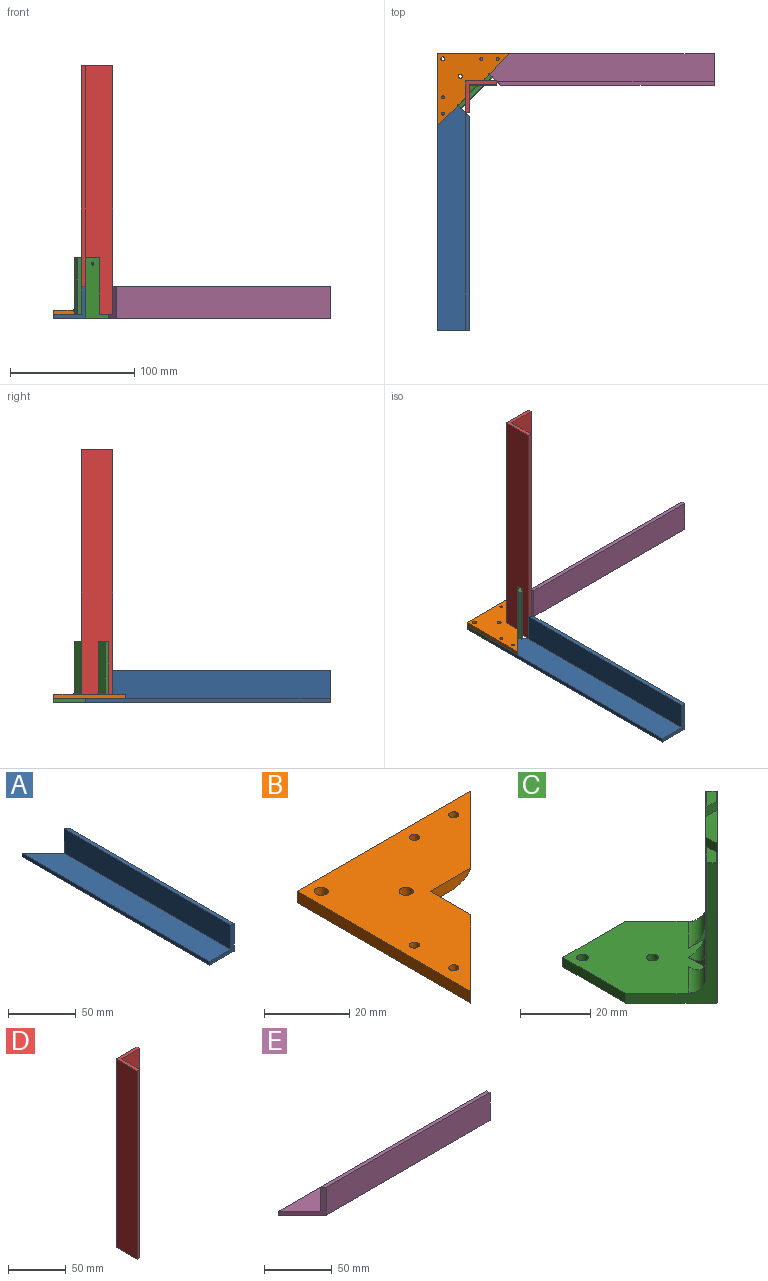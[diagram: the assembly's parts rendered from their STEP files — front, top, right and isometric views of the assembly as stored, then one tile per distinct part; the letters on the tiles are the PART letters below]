
ASSEMBLY  parts=5 mates=4
PART A: 8 faces, bbox 25.3x196.8x25.3 mm
  f0: plane 25.3x25.3mm, normal (0.71,0.71,0), area 214.5mm2, adj f2,f3,f4,f5,f6,f7
  f1: plane 25.3x25.3mm, normal (0,-1,0), area 151.7mm2, adj f2,f3,f4,f5,f6,f7
  f2: plane 174.7x3.2mm, normal (0,0,1), area 553.9mm2, adj f0,f1,f3,f7
  f3: plane 174.7x22.1mm, normal (-1,0,0), area 3860.9mm2, adj f0,f1,f2,f4
  f4: plane 196.8x22.1mm, normal (0,0,1), area 4105.1mm2, adj f0,f1,f3,f5
  f5: plane 196.8x3.2mm, normal (-1,0,0), area 629.8mm2, adj f0,f1,f4,f6
  f6: plane 196.8x25.3mm, normal (0,0,-1), area 4659mm2, adj f0,f1,f5,f7
  f7: plane 171.5x25.3mm, normal (1,0,0), area 4339mm2, adj f0,f1,f2,f6
PART B: 18 faces, bbox 57.7x57.7x3.3 mm
  f0: cylinder r=5mm len=12.56mm, axis (-0.71,-0.71,0), area 63.5mm2, adj f1,f5,f6,f9
  f1: plane 13.47x3.3mm, normal (1,0,0), area 38.5mm2, adj f0,f2,f5,f6
  f2: plane 13.47x3.3mm, normal (0,-1,0), area 38.5mm2, adj f1,f5,f6,f7
  f3: plane 57.67x3.3mm, normal (0,1,0), area 190.3mm2, adj f4,f5,f6,f11
  f4: plane 57.67x3.3mm, normal (-1,0,0), area 190.3mm2, adj f3,f5,f6,f8
  f5: plane 57.67x57.67mm, normal (0,0,1), area 1537mm2, adj f0,f1,f2,f3,f4,f7,f8,f11
  f6: plane 57.67x57.67mm, normal (0,0,-1), area 1436.3mm2, adj f0,f1,f2,f3,f4,f7,f8,f9
  f7: cylinder r=5mm len=12.56mm, axis (0.71,0.71,0), area 63.5mm2, adj f2,f5,f6,f10
  f8: plane 16.19x16.19mm, normal (0.71,-0.71,0), area 75.5mm2, adj f4,f5,f6,f9
  f9: plane 3.33x3.33mm, normal (0.71,0.71,0), area 4.2mm2, adj f0,f6,f8
  f10: plane 3.33x3.33mm, normal (-0.71,-0.71,0), area 4.2mm2, adj f6,f7,f11
  f11: plane 16.19x16.19mm, normal (0.71,-0.71,0), area 75.5mm2, adj f3,f5,f6,f10
  f12: cylinder r=1.65mm len=3.3mm, axis (0,0,1), area 34.2mm2, adj f5,f6
  f13: cylinder r=1.65mm len=3.3mm, axis (0,0,1), area 34.2mm2, adj f5,f6
  f14: cylinder r=1.2mm len=3.3mm, axis (0,0,1), area 24.9mm2, adj f5,f6
  f15: cylinder r=1.2mm len=3.3mm, axis (0,0,1), area 24.9mm2, adj f5,f6
  f16: cylinder r=1.2mm len=3.3mm, axis (0,0,1), area 24.9mm2, adj f5,f6
  f17: cylinder r=1.2mm len=3.3mm, axis (0,0,1), area 24.9mm2, adj f5,f6
PART C: 39 faces, bbox 48.3x48.3x49.1 mm
  f0: plane 40.24x40.24mm, normal (0,0,1), area 1018.2mm2, adj f1,f2,f3,f4,f5,f7,f8,f11
  f1: plane 48.75x18.34mm, normal (-0.71,-0.71,0), area 219.2mm2, adj f0,f5,f6,f21,f24,f26,f37
  f2: plane 49x24.95mm, normal (0.71,-0.71,0), area 1308.1mm2, adj f0,f6,f7,f8,f10,f11,f14,f19
  f3: plane 48.75x18.34mm, normal (0.71,0.71,0), area 219.2mm2, adj f0,f4,f6,f27,f30,f33,f35
  f4: plane 25.3x3.3mm, normal (0,1,0), area 83.5mm2, adj f0,f3,f5,f6
  f5: plane 25.3x3.3mm, normal (-1,0,0), area 83.5mm2, adj f0,f1,f4,f6
  f6: plane 43.72x43.72mm, normal (0,0,-1), area 1240mm2, adj f1,f2,f3,f4,f5,f17,f18,f21
  f7: plane 45.7x11.74mm, normal (-1,0,0), area 220.9mm2, adj f0,f2,f9,f10,f38
  f8: plane 45.7x11.74mm, normal (0,1,0), area 220.9mm2, adj f0,f2,f9,f10,f38
  f9: plane 40.7x7.07mm, normal (-0.71,0.71,0), area 402.5mm2, adj f7,f8,f10,f19,f38
  f10: plane 11.74x11.74mm, normal (0,0,1), area 43.9mm2, adj f2,f7,f8,f9
  f11: plane 45.81x11.84mm, normal (0,-1,0), area 220.8mm2, adj f0,f2,f12,f13,f28,f31,f34
  f12: plane 40.45x5.74mm, normal (-0.71,0.71,0), area 328.2mm2, adj f11,f31,f33,f34
  f13: plane 7.54x5.56mm, normal (0,0,1), area 18.1mm2, adj f11,f28,f30,f31
  f14: plane 45.81x11.84mm, normal (1,0,0), area 220.8mm2, adj f0,f2,f15,f16,f20,f23,f36
  f15: plane 40.45x5.74mm, normal (-0.71,0.71,0), area 328.2mm2, adj f14,f23,f26,f36
  f16: plane 7.54x5.56mm, normal (0,0,1), area 18.1mm2, adj f14,f20,f23,f24
  f17: cylinder r=1.65mm len=3.3mm, axis (0,0,-1), area 34.2mm2, adj f0,f6
  f18: cylinder r=1.65mm len=3.3mm, axis (0,0,-1), area 34.2mm2, adj f0,f6
  f19: cylinder r=1.2mm len=4.03mm, axis (0.71,-0.71,0), area 24.9mm2, adj f2,f9
  f20: cylinder r=0.25mm len=3.76mm, axis (-0.71,-0.71,0), area 1.9mm2, adj f2,f14,f16,f22
  f21: cylinder r=0.25mm len=48.75mm, axis (0,0,1), area 19.1mm2, adj f1,f2,f6,f22
  f22: sphere r=0.25mm, area 0.1mm2, adj f20,f21,f24
  f23: cylinder r=0.25mm len=5.91mm, axis (0.71,0.71,0), area 3.1mm2, adj f14,f15,f16,f25
  f24: cylinder r=0.25mm len=2.16mm, axis (-0.71,0.71,0), area 1.1mm2, adj f1,f16,f22,f25
  f25: sphere r=0.25mm, area 0.1mm2, adj f23,f24,f26
  f26: cylinder r=0.25mm len=40.45mm, axis (0,0,1), area 15.9mm2, adj f1,f15,f25,f37
  f27: cylinder r=0.25mm len=48.75mm, axis (0,0,-1), area 19.1mm2, adj f2,f3,f6,f29
  f28: cylinder r=0.25mm len=3.76mm, axis (-0.71,-0.71,0), area 1.9mm2, adj f2,f11,f13,f29
  f29: sphere r=0.25mm, area 0.1mm2, adj f27,f28,f30
  f30: cylinder r=0.25mm len=2.16mm, axis (0.71,-0.71,0), area 1.1mm2, adj f3,f13,f29,f32
  f31: cylinder r=0.25mm len=5.91mm, axis (0.71,0.71,0), area 3.1mm2, adj f11,f12,f13,f32
  f32: sphere r=0.25mm, area 0.1mm2, adj f30,f31,f33
  f33: cylinder r=0.25mm len=40.45mm, axis (0,0,1), area 15.9mm2, adj f3,f12,f32,f35
  f34: cylinder r=5mm len=12.81mm, axis (0.71,0.71,0), area 78mm2, adj f0,f11,f12,f35
  f35: torus R=5.25mm, axis (0,0,1), area 2.1mm2, adj f0,f3,f33,f34
  f36: cylinder r=5mm len=12.81mm, axis (0.71,0.71,0), area 78mm2, adj f0,f14,f15,f37
  f37: torus R=5.25mm, axis (0,0,1), area 2.1mm2, adj f0,f1,f26,f36
  f38: cylinder r=5mm len=10.61mm, axis (0.71,0.71,0), area 50mm2, adj f7,f8,f9
PART D: 8 faces, bbox 25.3x25.3x200 mm
  f0: plane 200x22.1mm, normal (0,-1,0), area 4420mm2, adj f1,f5,f6,f7
  f1: plane 200x3.2mm, normal (1,0,0), area 640mm2, adj f0,f2,f6,f7
  f2: plane 200x25.3mm, normal (0,1,0), area 5060mm2, adj f1,f3,f6,f7
  f3: plane 200x25.3mm, normal (-1,0,0), area 5060mm2, adj f2,f4,f6,f7
  f4: plane 200x3.2mm, normal (0,-1,0), area 640mm2, adj f3,f5,f6,f7
  f5: plane 200x22.1mm, normal (1,0,0), area 4420mm2, adj f0,f4,f6,f7
  f6: plane 25.3x25.3mm, normal (0,0,1), area 151.7mm2, adj f0,f1,f2,f3,f4,f5
  f7: plane 25.3x25.3mm, normal (0,0,-1), area 151.7mm2, adj f0,f1,f2,f3,f4,f5
PART E: 8 faces, bbox 196.8x25.3x25.3 mm
  f0: plane 25.3x25.3mm, normal (-0.71,-0.71,0), area 214.5mm2, adj f2,f3,f4,f5,f6,f7
  f1: plane 25.3x25.3mm, normal (1,0,0), area 151.7mm2, adj f2,f3,f4,f5,f6,f7
  f2: plane 174.7x3.2mm, normal (0,0,1), area 553.9mm2, adj f0,f1,f3,f7
  f3: plane 174.7x22.1mm, normal (0,1,0), area 3860.9mm2, adj f0,f1,f2,f4
  f4: plane 196.8x22.1mm, normal (0,0,1), area 4105.1mm2, adj f0,f1,f3,f5
  f5: plane 196.8x3.2mm, normal (0,1,0), area 629.8mm2, adj f0,f1,f4,f6
  f6: plane 196.8x25.3mm, normal (0,0,-1), area 4659mm2, adj f0,f1,f5,f7
  f7: plane 171.5x25.3mm, normal (0,-1,0), area 4339mm2, adj f0,f1,f2,f6
PLACE A t=(0,0,0.02)mm
PLACE B at identity
PLACE C at identity fixed
PLACE D at identity
PLACE E t=(0,0,0.02)mm
MATE fastened C.f1 <-> A.f0  axis (-0.71,-0.71,0) through (-22.1,-3.2,0)mm
MATE fastened E.f0 <-> C.f3  axis (-0.71,-0.71,0) through (3.2,22.1,0)mm
MATE fastened D.f7 <-> B.f6  axis (0,0,-1) through (0,0,3.3)mm
MATE fastened B.f6 <-> C.f0  axis (0,0,-1) through (-22.1,22.1,3.3)mm
